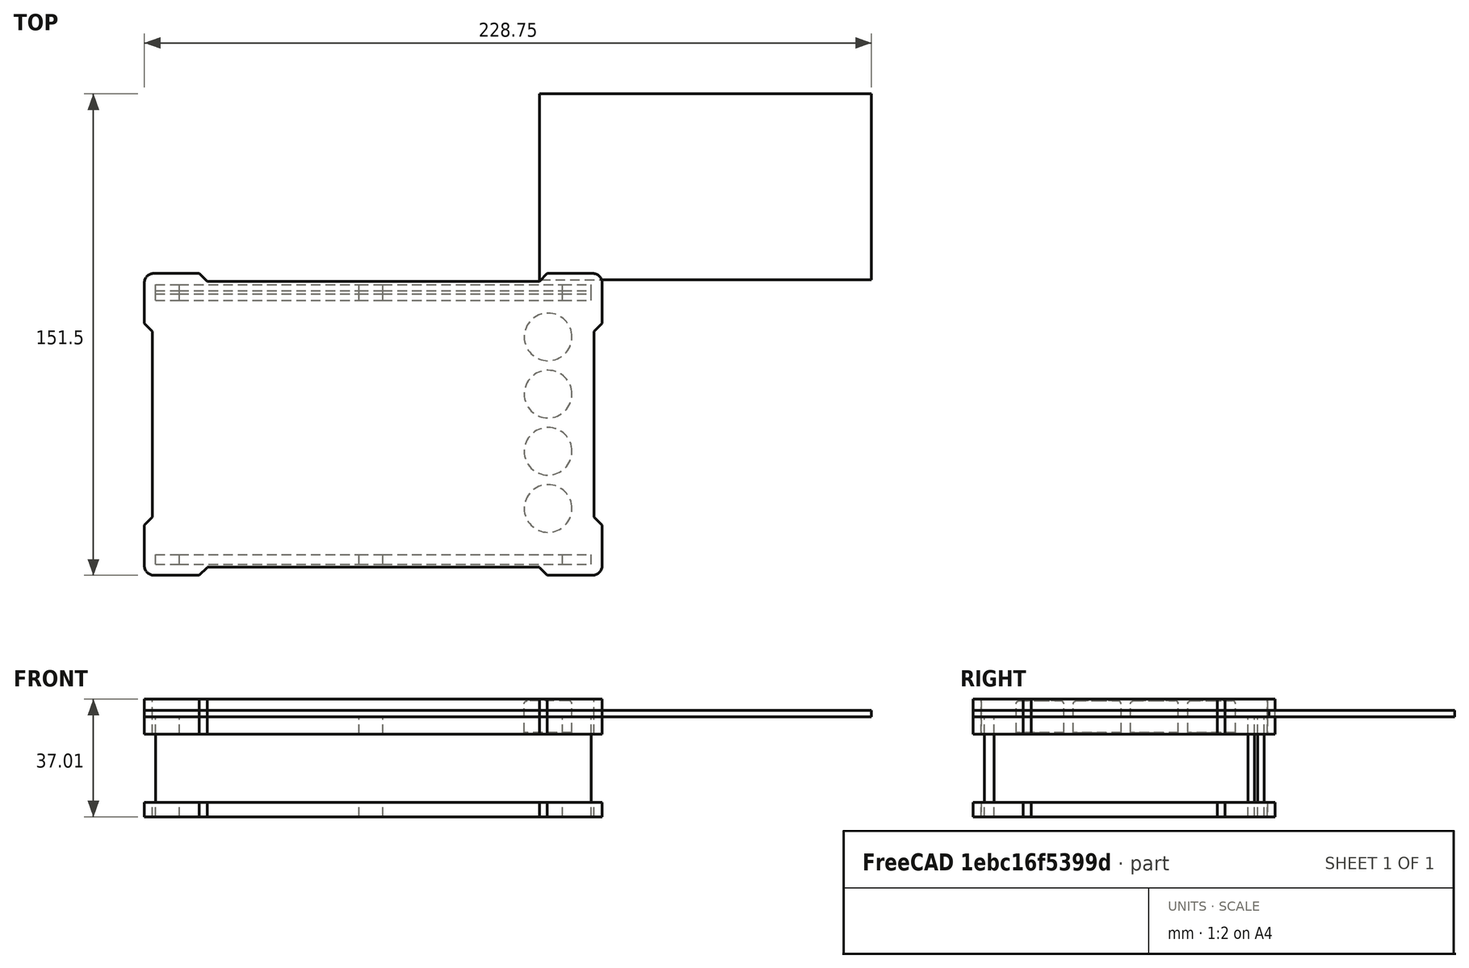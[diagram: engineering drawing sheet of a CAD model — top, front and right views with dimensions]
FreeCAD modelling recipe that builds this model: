
FCSTD DOCUMENT  (FreeCAD 0.17R13541 (Git))
Label: JOY6.5
License: All rights reserved
LicenseURL: http://en.wikipedia.org/wiki/All_rights_reserved
objects: Part::Box×16, Raytracing::RayFeature×9, Part::Fillet×5, Part::Feature×5, Part::Cylinder×4, Part::MultiFuse×3, Part::Cut×3, App::MeasureDistance×2, Part::Chamfer×1, Raytracing::RayProject×1
note: 37 computed .brp shape members not serialized (recipe doc carries the construction recipe); baked Part::Feature solids carry a one-line shape summary decoded from their .brp

FEATURE [Part::Box] Box  label="wai"
  AttacherType = Attacher::AttachEngine3D
  Height = 5.5
  Length = 144
  Placement = pos=(-72,-47.5,0) rot=(0,0,1;0rad)
  Width = 95
FEATURE [Part::Box] Box001  label="Cube001"
  AttacherType = Attacher::AttachEngine3D
  Height = 2
  Length = 104.5
  Placement = pos=(52.25,45.5,0) rot=(0,0,1;0rad)
  Width = 58.5
FEATURE [Part::Box] Box002  label="wai001"
  AttacherType = Attacher::AttachEngine3D
  Height = 5.5
  Length = 104.5
  Placement = pos=(-52.25,45,0) rot=(0,0,1;0rad)
  Width = 95
FEATURE [Part::Box] Box003  label="wai002"
  AttacherType = Attacher::AttachEngine3D
  Height = 5.5
  Length = 104.5
  Placement = pos=(-52.25,-140,0) rot=(0,0,1;0rad)
  Width = 95
FEATURE [Part::Box] Box004  label="wai003"
  AttacherType = Attacher::AttachEngine3D
  Height = 5.5
  Length = 144
  Placement = pos=(69.5,-29.25,0) rot=(0,0,1;0rad)
  Width = 58.5
FEATURE [Part::Box] Box005  label="wai004"
  AttacherType = Attacher::AttachEngine3D
  Height = 5.5
  Length = 144
  Placement = pos=(-213.5,-29.25,0) rot=(0,0,1;0rad)
  Width = 58.5
FEATURE [Part::MultiFuse] Fusion
  Shapes = -> [Box002,Box004,Box005,Box003]
FEATURE [Part::Cut] Cut
  Base = -> Box
  Tool = -> Fusion
FEATURE [Part::Chamfer] Chamfer
  Base = -> Cut
  Edges = 8 edges r=2.49: [Edge2,Edge44,Edge46,Edge48,Edge51,Edge53,Edge56,Edge58]
FEATURE [Part::Fillet] Fillet
  Base = -> Chamfer
  Edges = 4 edges r=3: [Edge3,Edge69,Edge72,Edge83]
FEATURE [Part::Feature] Fillet001  label="透明盖子"
  shape: bbox 144 x 95 x 2 mm, 34 faces (baked)
FEATURE [Part::Feature] Fillet002  label="黑色底盖子"
  Placement = pos=(0,0,-31.5) rot=(0,0,1;0rad)
  shape: bbox 144 x 95 x 4.5 mm, 34 faces (baked)
FEATURE [Part::Feature] Fillet003  label="黑色顶盖子"
  Placement = pos=(0,0,-5.5) rot=(0,0,1;0rad)
  shape: bbox 144 x 95 x 5.5 mm, 34 faces (baked)
FEATURE [Part::Cylinder] Cylinder
  Angle = 360
  AttacherType = Attacher::AttachEngine3D
  Height = 10
  Placement = pos=(55,27.5,-5) rot=(0,0,1;0rad)
  Radius = 7.5
FEATURE [Part::Fillet] Fillet004
  Base = -> Cylinder
  Edges = 1 edges r=1: [Edge1]
FEATURE [Part::Cylinder] Cylinder001
  Angle = 360
  AttacherType = Attacher::AttachEngine3D
  Height = 10
  Placement = pos=(55,9.5,-5) rot=(0,0,1;0rad)
  Radius = 7.5
FEATURE [Part::Fillet] Fillet005
  Base = -> Cylinder001
  Edges = 1 edges r=1: [Edge1]
FEATURE [Part::Cylinder] Cylinder002
  Angle = 360
  AttacherType = Attacher::AttachEngine3D
  Height = 10
  Placement = pos=(55,-8.5,-5) rot=(0,0,1;0rad)
  Radius = 7.5
FEATURE [Part::Fillet] Fillet006
  Base = -> Cylinder002
  Edges = 1 edges r=1: [Edge1]
FEATURE [Part::Cylinder] Cylinder003
  Angle = 360
  AttacherType = Attacher::AttachEngine3D
  Height = 10
  Placement = pos=(55,-26.5,-5) rot=(0,0,1;0rad)
  Radius = 7.5
FEATURE [Part::Fillet] Fillet007
  Base = -> Cylinder003
  Edges = 1 edges r=1: [Edge1]
FEATURE [Part::Box] Box006  label="Cube"
  AttacherType = Attacher::AttachEngine3D
  Height = 31.52
  Length = 137
  Placement = pos=(-68.5,50,-32.52) rot=(0,0,1;0rad)
  Width = 3
FEATURE [Part::Box] Box007  label="Cube002"
  AttacherType = Attacher::AttachEngine3D
  Height = 31
  Length = 56.5
  Placement = pos=(-61,50,-6.5) rot=(0,0,1;0rad)
  Width = 3
FEATURE [Part::Box] Box008  label="Cube003"
  AttacherType = Attacher::AttachEngine3D
  Height = 31
  Length = 56.5
  Placement = pos=(3,50,-6.5) rot=(0,0,1;0rad)
  Width = 3
FEATURE [Part::Box] Box009  label="Cube004"
  AttacherType = Attacher::AttachEngine3D
  Height = 31
  Length = 56.5
  Placement = pos=(-61,50,-59) rot=(0,0,1;0rad)
  Width = 3
FEATURE [Part::Box] Box010  label="Cube005"
  AttacherType = Attacher::AttachEngine3D
  Height = 31
  Length = 56.5
  Placement = pos=(3,50,-59) rot=(0,0,1;0rad)
  Width = 3
FEATURE [Part::MultiFuse] Fusion001
  Shapes = -> [Box008,Box009,Box010,Box007]
FEATURE [Part::Cut] Cut001
  Base = -> Box006
  Placement = pos=(0,-11,1.01) rot=(0,0,1;0rad)
  Tool = -> Fusion001
FEATURE [Part::Box] Box016  label="Cube011"
  AttacherType = Attacher::AttachEngine3D
  Height = 31.52
  Length = 137
  Placement = pos=(-68.5,50,-32.52) rot=(0,0,1;0rad)
  Width = 3
FEATURE [Part::Box] Box017  label="Cube012"
  AttacherType = Attacher::AttachEngine3D
  Height = 31
  Length = 56.5
  Placement = pos=(-61,50,-59) rot=(0,0,1;0rad)
  Width = 3
FEATURE [Part::Box] Box018  label="Cube013"
  AttacherType = Attacher::AttachEngine3D
  Height = 31
  Length = 56.5
  Placement = pos=(3,50,-59) rot=(0,0,1;0rad)
  Width = 3
FEATURE [Part::Box] Box019  label="Cube014"
  AttacherType = Attacher::AttachEngine3D
  Height = 31
  Length = 56.5
  Placement = pos=(-61,50,-6.5) rot=(0,0,1;0rad)
  Width = 3
FEATURE [Part::Box] Box020  label="Cube015"
  AttacherType = Attacher::AttachEngine3D
  Height = 31
  Length = 56.5
  Placement = pos=(3,50,-6.5) rot=(0,0,1;0rad)
  Width = 3
FEATURE [Part::MultiFuse] Fusion003
  Shapes = -> [Box020,Box017,Box018,Box019]
FEATURE [Part::Cut] Cut003
  Base = -> Box016
  Placement = pos=(0,-11,1.01) rot=(0,0,1;0rad)
  Tool = -> Fusion003
FEATURE [Part::Feature] Cut001001  label="Cut004"
  Placement = pos=(0,-9,1.01) rot=(0,0,1;0rad)
  shape: bbox 137 x 3 x 31.52 mm, 22 faces (baked)
FEATURE [Part::Feature] Cut001002  label="Cut005"
  Placement = pos=(0,-94,1.01) rot=(0,0,1;0rad)
  shape: bbox 137 x 3 x 31.52 mm, 22 faces (baked)
FEATURE [App::MeasureDistance] Distance  label="Distance: 3.00 mm"
  Distance = 3.00253
  P1 = (-5.35886,42.0323,-5.5)
  P2 = (-5.84291,44.9956,-5.5)
FEATURE [App::MeasureDistance] Distance001  label="Distance: 0.99 mm"
  Distance = 0.992418
  P1 = (-0.0690353,44,0.00999999)
  P2 = (0.272085,44.9319,0)
FEATURE [Raytracing::RayFeature] Cut001002_View
  Result = <blob: 11255 chars omitted>
  Source = -> Cut001002
  Transparency = 0
FEATURE [Raytracing::RayFeature] Cut001001_View
  Result = <blob: 11135 chars omitted>
  Source = -> Cut001001
  Transparency = 0
FEATURE [Raytracing::RayFeature] Fillet007_View
  Result = <blob: 43711 chars omitted>
  Source = -> Fillet007
  Transparency = 0
FEATURE [Raytracing::RayFeature] Fillet006_View
  Result = <blob: 43690 chars omitted>
  Source = -> Fillet006
  Transparency = 0
FEATURE [Raytracing::RayFeature] Fillet004_View
  Result = <blob: 43346 chars omitted>
  Source = -> Fillet004
  Transparency = 0
FEATURE [Raytracing::RayFeature] Fillet005_View
  Result = <blob: 43217 chars omitted>
  Source = -> Fillet005
  Transparency = 0
FEATURE [Raytracing::RayFeature] Fillet003_View
  Result = <blob: 24341 chars omitted>
  Source = -> Fillet003
  Transparency = 0
FEATURE [Raytracing::RayFeature] Fillet002_View
  Result = <blob: 24786 chars omitted>
  Source = -> Fillet002
  Transparency = 50
FEATURE [Raytracing::RayFeature] Fillet001_View
  Result = <blob: 23901 chars omitted>
  Source = -> Fillet001
  Transparency = 50
FEATURE [Raytracing::RayProject] PovProject
  Camera = // declares position and view direction\n\n// Generated by FreeCAD (http://www.freecadweb.org/)\n#declare cam_location =  <5.67494,283.203,-81.3739>;\n#declare cam_look_at  = <34.0833,76.9609,-18.5023>;\n#declare cam_sky      = <-0.237927,0.253089,0.93773>;\n#declare cam_angle    = 45; \ncamera {\n  location  cam_location\n  look_at   cam_look_at\n  sky       cam_sky\n  angle     cam_angle \n  right x*800/600\n}
  Group = -> [Cut001002_View,Cut001001_View,Fillet007_View,Fillet006_View,Fillet004_View,Fillet005_View,Fillet003_View,Fillet002_View,Fillet001_View]
  Template = <path>
note: 1 file-system path scrubbed to <path> (originals preserved in the JSON sidecar)
